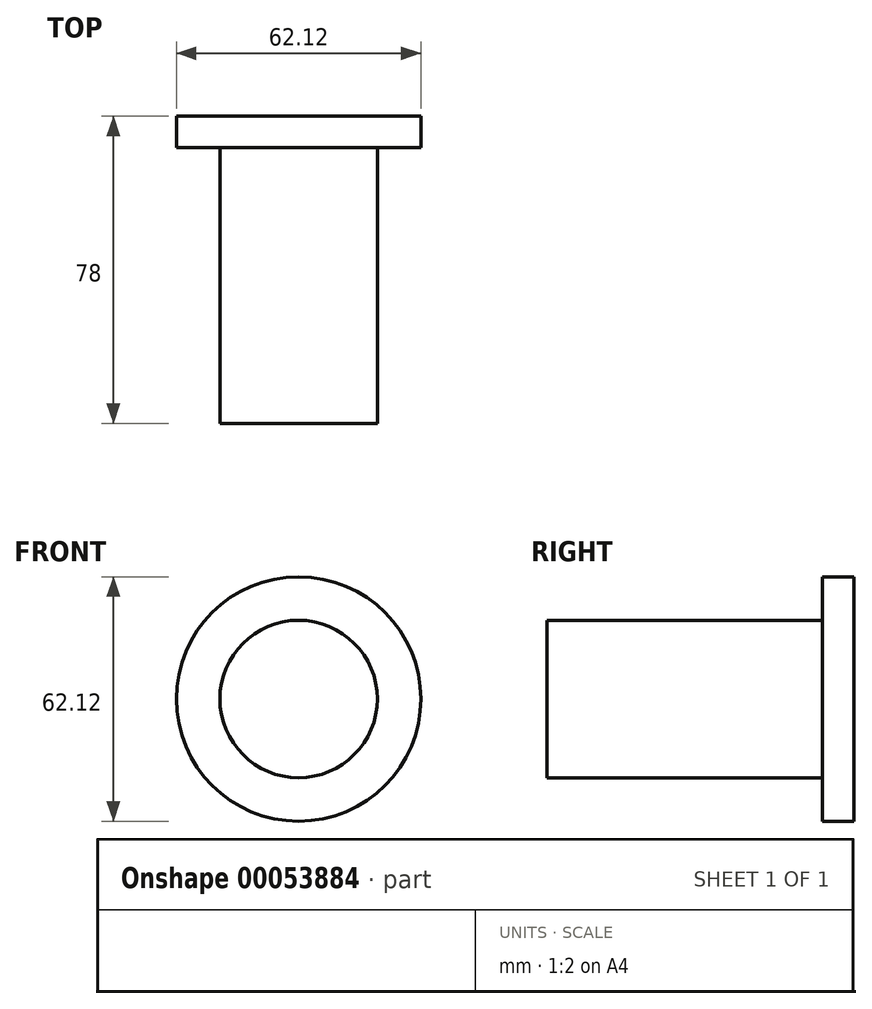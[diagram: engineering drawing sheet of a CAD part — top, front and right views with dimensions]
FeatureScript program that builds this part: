
annotation { "Feature Type Name" : "Feature", "Feature Type Description" : "" }
export const myFeature = defineFeature(function(context is Context, id is Id, definition is map)
    precondition{}
    {
        {
            var Q0;
            Q0=qCreatedBy(makeId("Front.planeOp"),FACE);
            var sketch = newSketch(context, id + "F0", { "sketchPlane" : qUnion([Q0])});
            skCircle(sketch, "E0", {"center": v(0, 0) * mm, "radius": 20 * mm});
            skSolve(sketch);
        }
        {
            var Q0;
            Q0=makeQuery(id+"F0.imprint","IMPRINT",FACE,{"disambiguationData":[TD([[makeQuery(id+"F0.imprint","IMPRINT",EDGE,{"derivedFrom":sQuery(id+"F0.wireOp",EDGE,"E0")}),1.0]])]});
            extrude(context, id + "F1", {"entities" : qUnion([Q0]), "depth" : 70 * mm});
        }
        {
            var Q0;
            Q0=makeQuery(id+"F1.opExtrude","CAP_FACE",FACE,{"disambiguationData":[OSD([sQuery(id+"F0.wireOp",EDGE,"E0")])],"isStart":true});
            var sketch = newSketch(context, id + "F2", { "sketchPlane" : qUnion([Q0])});
            skCircle(sketch, "E1", {"center": v(0, 0) * mm, "radius": 31.06 * mm});
            skSolve(sketch);
        }
        {
            var Q0;
            Q0=makeQuery(id+"F2.imprint","IMPRINT",FACE,{"disambiguationData":[TD([[makeQuery(id+"F2.imprint","IMPRINT",EDGE,{"derivedFrom":makeQuery(id+"F1.opExtrude","CAP_EDGE",EDGE,{"disambiguationData":[OSD([sQuery(id+"F0.wireOp",EDGE,"E0")])],"isStart":true})}),-1.0]])]});
            var Q1;
            Q1=makeQuery(id+"F2.imprint","IMPRINT",FACE,{"disambiguationData":[TD([[makeQuery(id+"F2.imprint","IMPRINT",EDGE,{"derivedFrom":sQuery(id+"F2.wireOp",EDGE,"E1")}),1.0]])]});
            extrude(context, id + "F3", {"entities" : qUnion([Q0, Q1]), "operationType" : NewBodyOperationType.ADD, "depth" : 8 * mm});
        }
    });
